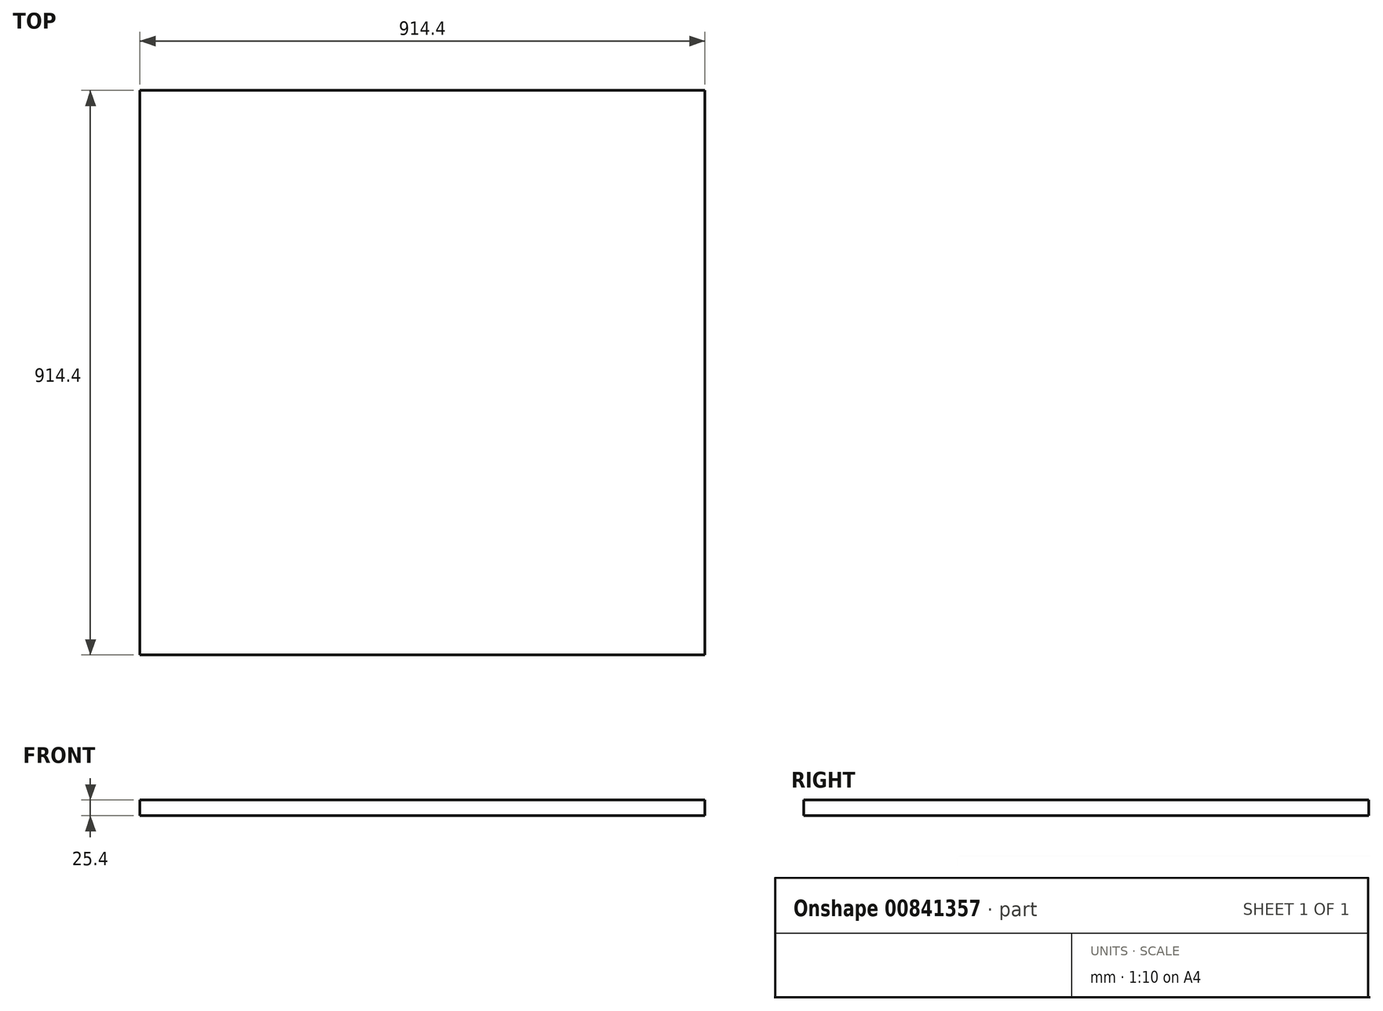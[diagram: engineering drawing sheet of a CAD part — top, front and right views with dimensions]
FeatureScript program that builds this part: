
annotation { "Feature Type Name" : "Feature", "Feature Type Description" : "" }
export const myFeature = defineFeature(function(context is Context, id is Id, definition is map)
    precondition{}
    {
        {
            var Q0;
            Q0=qCreatedBy(makeId("Top.planeOp"),FACE);
            var sketch = newSketch(context, id + "F0", { "sketchPlane" : qUnion([Q0])});
            skLineSegment(sketch, "E0.bottom", {"start": v(-445.8, -345.4) * mm, "end": v(468.6, -345.4) * mm});
            skLineSegment(sketch, "E0.top", {"start": v(-445.8, 569) * mm, "end": v(468.6, 569) * mm});
            skLineSegment(sketch, "E0.left", {"start": v(-445.8, -345.4) * mm, "end": v(-445.8, 569) * mm});
            skLineSegment(sketch, "E0.right", {"start": v(468.6, -345.4) * mm, "end": v(468.6, 569) * mm});
            skSolve(sketch);
        }
        {
            var Q0;
            Q0=sQuery(id+"F0.wireOp",EDGE,"E0.bottom");
            var Q1;
            Q1=sQuery(id+"F0.wireOp",EDGE,"E0.right");
            var Q2;
            Q2=sQuery(id+"F0.wireOp",EDGE,"E0.top");
            var Q3;
            Q3=sQuery(id+"F0.wireOp",EDGE,"E0.left");
            extrude(context, id + "F1", {"bodyType" : ToolBodyType.SURFACE, "surfaceEntities" : qUnion([Q0, Q1, Q2, Q3]), "depth" : 25.4 * mm, "offsetDistance" : 25.4 * mm});
        }
    });
